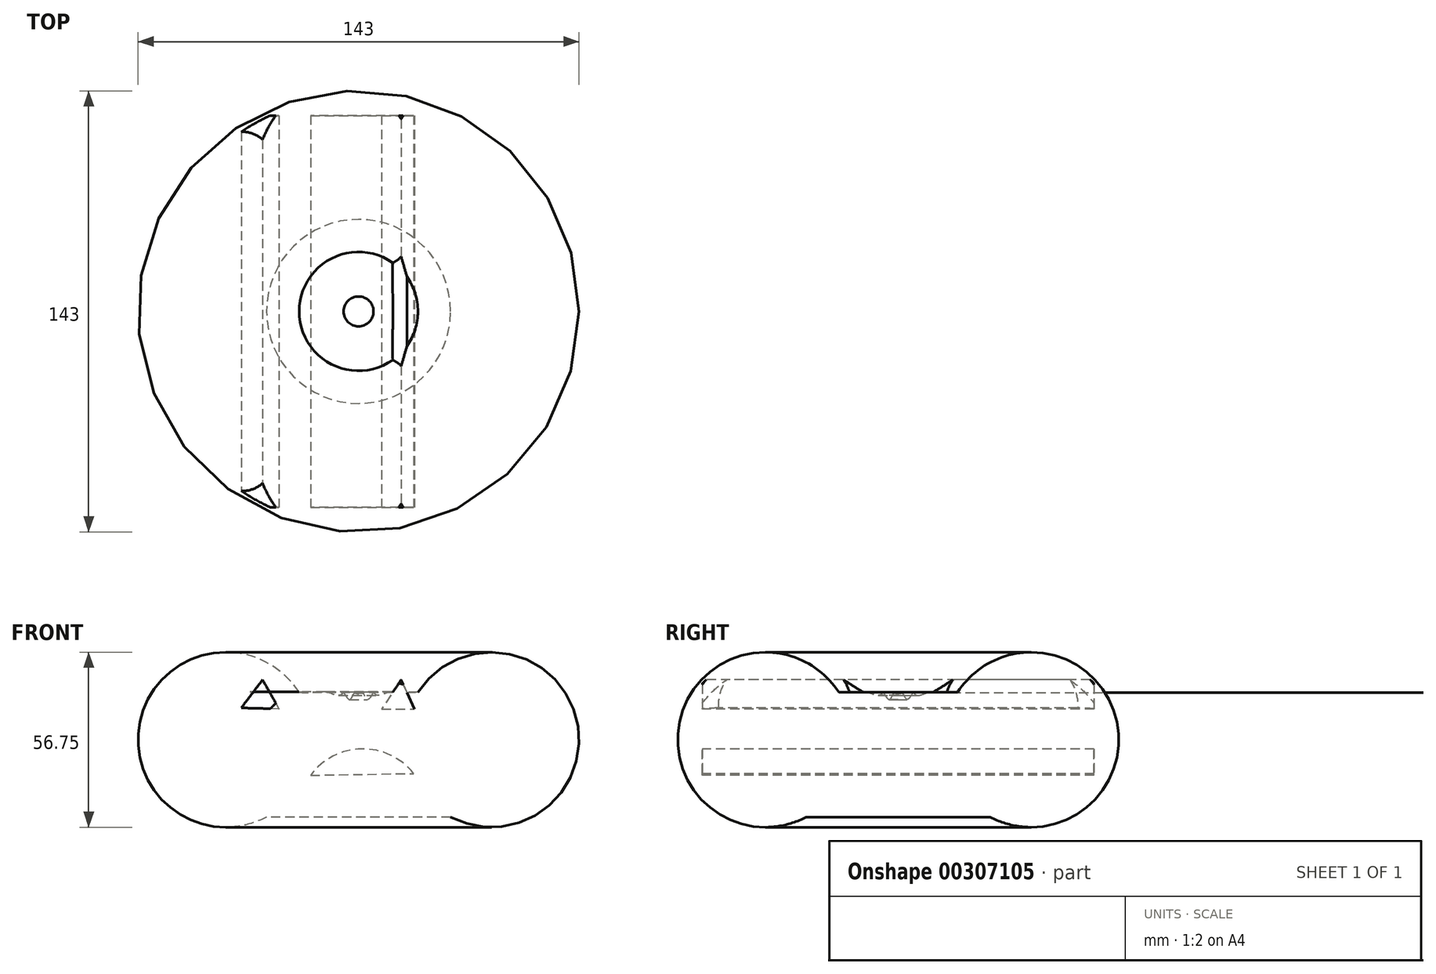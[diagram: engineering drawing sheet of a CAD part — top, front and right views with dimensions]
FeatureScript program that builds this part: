
annotation { "Feature Type Name" : "Feature", "Feature Type Description" : "" }
export const myFeature = defineFeature(function(context is Context, id is Id, definition is map)
    precondition{}
    {
        {
            var Q0;
            Q0=qCreatedBy(makeId("Front.planeOp"),FACE);
            var sketch = newSketch(context, id + "F0", { "sketchPlane" : qUnion([Q0])});
            skLineSegment(sketch, "E0", {"start": v(0, 81.3) * mm, "end": v(0, -87.62) * mm});
            skLineSegment(sketch, "E1", {"start": v(0, 0) * mm, "end": v(29.83, 0) * mm});
            skArc(sketch, "E2", {"start": v(29.83, 0) * mm, "mid": v(70.58, 32.24) * mm, "end": v(19.27, 40.41) * mm});
            skFitSpline(sketch, "E3", {"points": [v(19.27, 40.41) * mm, v(12.43, 40.41) * mm, v(9.74, 40.41) * mm, v(6.41, 39.4) * mm, v(4.85, 40.41) * mm], "startDerivative": vector(-22.12, -0.56) * mm, "endDerivative": vector(-7.35, 8) * mm});
            skFitSpline(sketch, "E4", {"points": [v(4.85, 40.41) * mm, v(2.75, 38.1) * mm, v(1.58, 39.93) * mm, v(0, 39.93) * mm], "startDerivative": vector(-5.99, -9.66) * mm, "endDerivative": vector(-6.25, -2) * mm});
            skSolve(sketch);
        }
        {
            var Q0;
            {var subQ0=sQuery(id+"F0.wireOp",EDGE,"E1");Q0=makeQuery(id+"F0.imprint","IMPRINT",FACE,{"disambiguationData":[TD([[makeQuery(id+"F0.imprint","IMPRINT",EDGE,{"derivedFrom":subQ0}),1.0]])]});}
            var Q1;
            Q1=sQuery(id+"F0.wireOp",EDGE,"E0");
            revolve(context, id + "F1", {"entities" : qUnion([Q0]), "axis" : qUnion([Q1]), "revolveType" : RevolveType.FULL});
        }
        {
            var Q0;
            Q0=qCreatedBy(makeId("Front.planeOp"),FACE);
            var sketch = newSketch(context, id + "F2", { "sketchPlane" : qUnion([Q0])});
            skLineSegment(sketch, "E5", {"start": v(-31.12, 44.48) * mm, "end": v(-38.04, 35.37) * mm});
            skLineSegment(sketch, "E6", {"start": v(-31.12, 44.48) * mm, "end": v(-25.78, 35.05) * mm});
            skLineSegment(sketch, "E7", {"start": v(-25.78, 35.05) * mm, "end": v(-38.04, 35.37) * mm});
            skArc(sketch, "E8", {"start": v(17.84, 14.1) * mm, "mid": v(1, 22.08) * mm, "end": v(-15.54, 13.53) * mm});
            skLineSegment(sketch, "E9", {"start": v(-15.54, 13.53) * mm, "end": v(17.84, 14.1) * mm});
            skLineSegment(sketch, "E10", {"start": v(7.48, 35.05) * mm, "end": v(18.13, 35.05) * mm});
            skLineSegment(sketch, "E11", {"start": v(13.81, 44.48) * mm, "end": v(7.48, 35.05) * mm});
            skLineSegment(sketch, "E12", {"start": v(13.81, 44.48) * mm, "end": v(18.13, 35.05) * mm});
            skSolve(sketch);
        }
        {
            var Q0;
            Q0 = qSketchRegion(id + "F2", true);
            extrude(context, id + "F3", {"entities" : qUnion([Q0]), "operationType" : NewBodyOperationType.REMOVE, "endBound" : BoundingType.SYMMETRIC, "oppositeDirection" : true, "depth" : 127 * mm});
        }
    });
